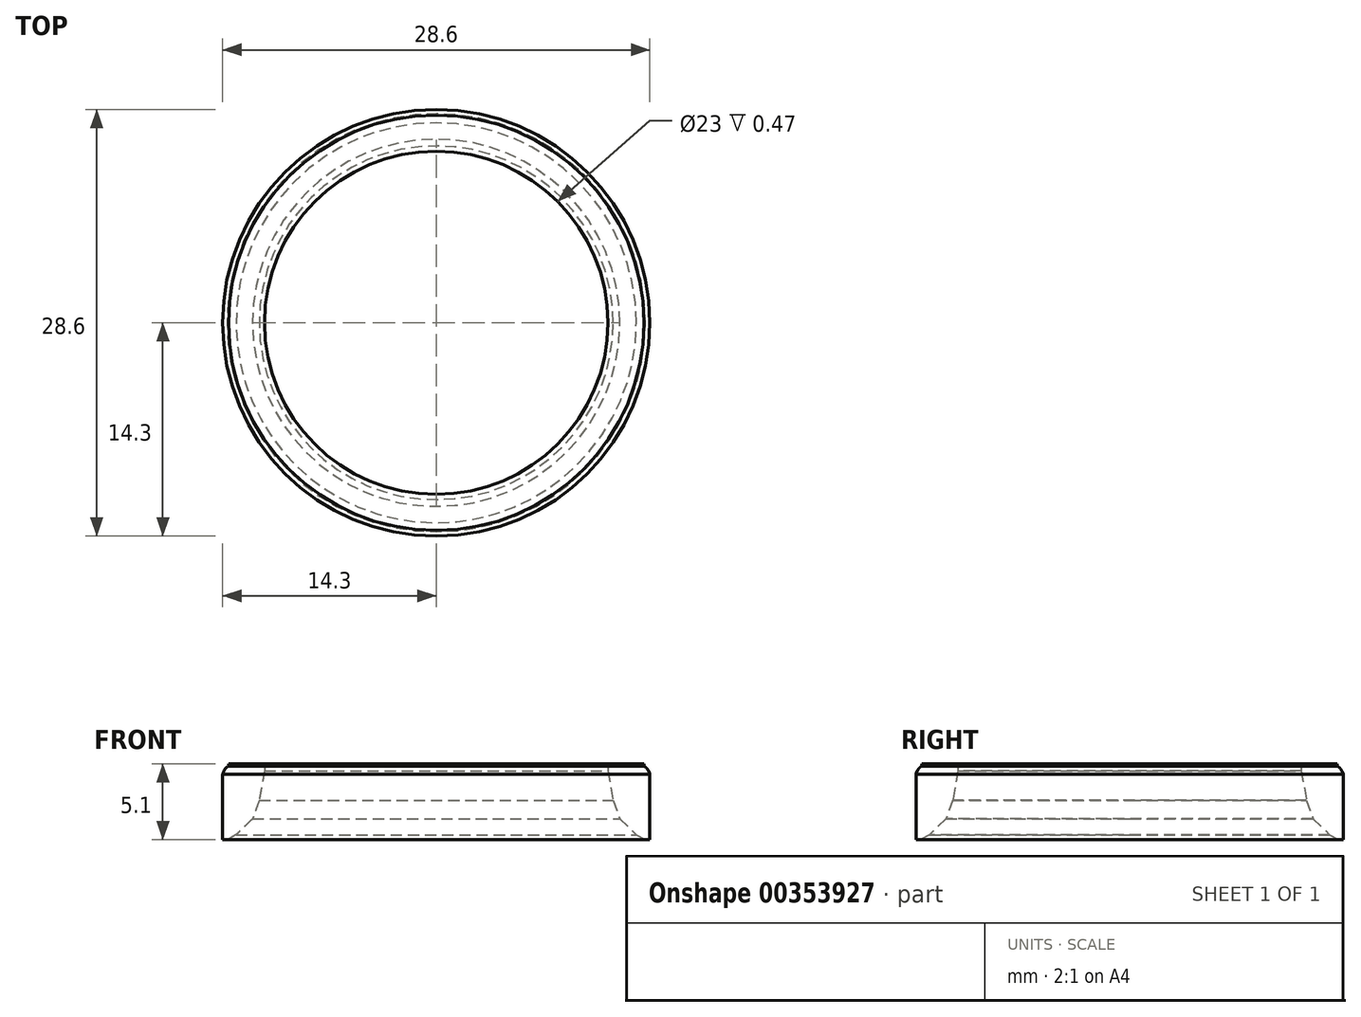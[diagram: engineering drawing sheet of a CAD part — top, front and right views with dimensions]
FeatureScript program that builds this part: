
annotation { "Feature Type Name" : "Feature", "Feature Type Description" : "" }
export const myFeature = defineFeature(function(context is Context, id is Id, definition is map)
    precondition{}
    {
        {
            var Q0;
            Q0=qCreatedBy(makeId("Front.planeOp"),FACE);
            var sketch = newSketch(context, id + "F0", { "sketchPlane" : qUnion([Q0])});
            skLineSegment(sketch, "E0", {"start": v(0, -5.16) * mm, "end": v(0, 19.29) * mm, "construction": true});
            skLineSegment(sketch, "E1", {"start": v(13.55, 0.5) * mm, "end": v(11.48, 2.5) * mm});
            skLineSegment(sketch, "E2", {"start": v(11.48, 2.5) * mm, "end": v(7.61, 3.08) * mm});
            skLineSegment(sketch, "E3", {"start": v(2.5, 100) * mm, "end": v(2.5, 9.01) * mm});
            skLineSegment(sketch, "E4", {"start": v(13.55, 0.5) * mm, "end": v(13.55, 0.2) * mm});
            skLineSegment(sketch, "E5", {"start": v(13.55, 0.2) * mm, "end": v(13.35, 0) * mm});
            skLineSegment(sketch, "E6", {"start": v(13.35, 0) * mm, "end": v(0, 0) * mm});
            skLineSegment(sketch, "E7", {"start": v(2.5, 100) * mm, "end": v(0, 100) * mm});
            skLineSegment(sketch, "E8", {"start": v(0, 100) * mm, "end": v(0, 0) * mm});
            skArc(sketch, "E9", {"start": v(2.5, 9.01) * mm, "mid": v(3.95, 5.1) * mm, "end": v(7.61, 3.08) * mm});
            skLineSegment(sketch, "E10", {"start": v(11.5, 5.4) * mm, "end": v(11.5, 4.93) * mm});
            skLineSegment(sketch, "E11", {"start": v(11.5, 4.93) * mm, "end": v(11.85, 2.94) * mm});
            skLineSegment(sketch, "E12", {"start": v(11.85, 2.94) * mm, "end": v(12.3, 1.7) * mm});
            skLineSegment(sketch, "E13", {"start": v(12.3, 1.7) * mm, "end": v(13.4, 0.64) * mm});
            skLineSegment(sketch, "E14", {"start": v(14, 0.3) * mm, "end": v(13.4, 0.64) * mm});
            skLineSegment(sketch, "E15", {"start": v(13.91, 5.4) * mm, "end": v(11.5, 5.4) * mm});
            skLineSegment(sketch, "E16", {"start": v(14, 0.3) * mm, "end": v(14.3, 0.3) * mm});
            skLineSegment(sketch, "E17", {"start": v(14.3, 0.3) * mm, "end": v(14.3, 4.7) * mm});
            skArc(sketch, "E18", {"start": v(14.25, 4.84) * mm, "mid": v(14.12, 5.07) * mm, "end": v(13.91, 5.25) * mm});
            skLineSegment(sketch, "E19", {"start": v(13.91, 5.25) * mm, "end": v(13.91, 5.4) * mm});
            skLineSegment(sketch, "E20", {"start": v(14.3, 4.7) * mm, "end": v(14.25, 4.84) * mm});
            skSolve(sketch);
        }
        {
            var Q0;
            Q0=makeQuery(id+"F0.imprint","IMPRINT",FACE,{"disambiguationData":[TD([[makeQuery(id+"F0.imprint","IMPRINT",EDGE,{"derivedFrom":sQuery(id+"F0.wireOp",EDGE,"E10")}),1.0]])]});
            var Q1;
            Q1=sQuery(id+"F0.wireOp",EDGE,"E0");
            revolve(context, id + "F1", {"surfaceOperationType" : NewSurfaceOperationType.NEW, "entities" : qUnion([Q0]), "axis" : qUnion([Q1]), "revolveType" : RevolveType.FULL});
        }
    });
